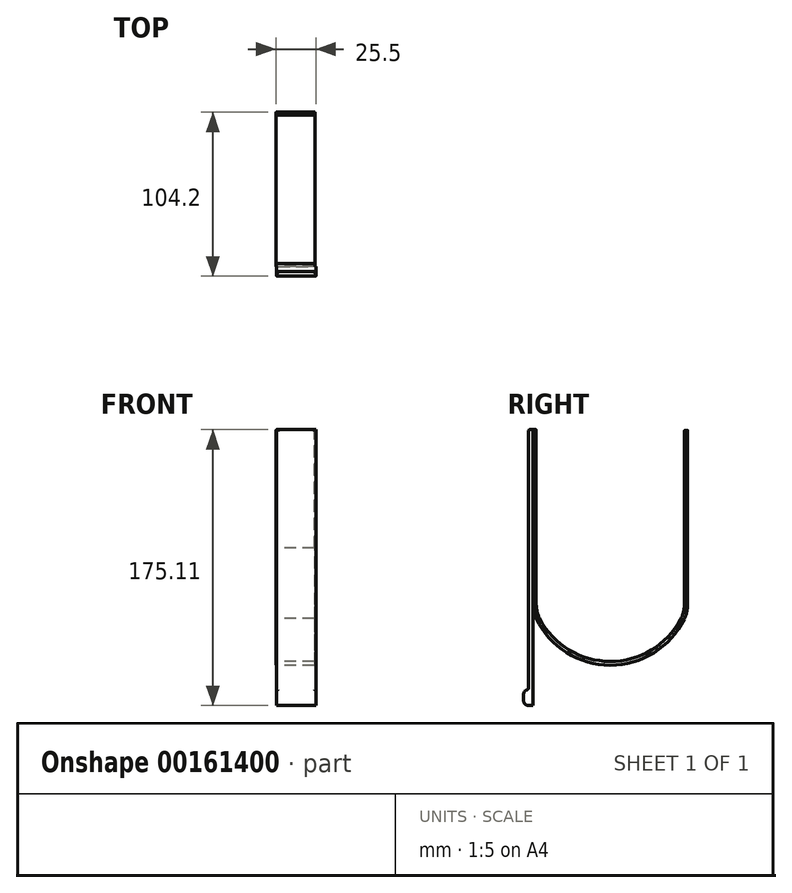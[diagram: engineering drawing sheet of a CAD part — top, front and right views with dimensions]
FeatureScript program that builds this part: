
annotation { "Feature Type Name" : "Feature", "Feature Type Description" : "" }
export const myFeature = defineFeature(function(context is Context, id is Id, definition is map)
    precondition{}
    {
        {
            var Q0;
            Q0=qCreatedBy(makeId("Right.planeOp"),FACE);
            var sketch = newSketch(context, id + "F0", { "sketchPlane" : qUnion([Q0])});
            skLineSegment(sketch, "E0.top", {"start": v(-75, -0.1) * mm, "end": v(-75, -0.1) * mm});
            skLineSegment(sketch, "E1", {"start": v(23.2, -0.2) * mm, "end": v(23.2, 74.65) * mm});
            skLineSegment(sketch, "E2", {"start": v(21.2, 17) * mm, "end": v(21.2, 74.65) * mm});
            skLineSegment(sketch, "E3", {"start": v(21.2, 74.65) * mm, "end": v(23.2, 74.65) * mm});
            skLineSegment(sketch, "E4.right", {"start": v(-73, -0.1) * mm, "end": v(-73, -0.1) * mm});
            skLineSegment(sketch, "E5.left", {"start": v(-75, -0.1) * mm, "end": v(-75, 19.67) * mm});
            skLineSegment(sketch, "E6.top", {"start": v(-75, 75.06) * mm, "end": v(-73, 75.06) * mm});
            skPoint(sketch, "E5.right.end.orphan", {"position": v(-73, -27.9) * mm});
            skPoint(sketch, "E7.orphan", {"position": v(73, 0) * mm});
            skLineSegment(sketch, "E8", {"start": v(21.2, -0.2) * mm, "end": v(21.2, 17) * mm});
            skLineSegment(sketch, "E9", {"start": v(-75, 19.67) * mm, "end": v(-75, 75.06) * mm});
            skLineSegment(sketch, "E10", {"start": v(-73, -0.1) * mm, "end": v(-73, 75.06) * mm});
            skLineSegment(sketch, "E11", {"start": v(-75, -0.1) * mm, "end": v(-75, -36.03) * mm});
            skLineSegment(sketch, "E12", {"start": v(-73, -0.1) * mm, "end": v(-73, -35.72) * mm});
            skLineSegment(sketch, "E13", {"start": v(21.11, -36.05) * mm, "end": v(21.2, -0.2) * mm});
            skLineSegment(sketch, "E14", {"start": v(23.2, -0.2) * mm, "end": v(23.11, -36.36) * mm});
            skPoint(sketch, "E15.visualSharp", {"position": v(-73, -40.17) * mm});
            skArc(sketch, "E15.filletArc", {"start": v(-73, -35.72) * mm, "mid": v(-72.4, -40.59) * mm, "end": v(-70.63, -45.16) * mm});
            skPoint(sketch, "E16.visualSharp", {"position": v(-75, -40.17) * mm});
            skArc(sketch, "E16.filletArc", {"start": v(-75, -36.03) * mm, "mid": v(-74.48, -40.55) * mm, "end": v(-72.95, -44.85) * mm});
            skPoint(sketch, "E17.visualSharp", {"position": v(21.1, -40.47) * mm});
            skArc(sketch, "E17.filletArc", {"start": v(18.75, -45.43) * mm, "mid": v(20.5, -40.88) * mm, "end": v(21.11, -36.05) * mm});
            skPoint(sketch, "E18.visualSharp", {"position": v(23.1, -40.47) * mm});
            skArc(sketch, "E18.filletArc", {"start": v(21.07, -45.11) * mm, "mid": v(22.59, -40.85) * mm, "end": v(23.11, -36.36) * mm});
            skArc(sketch, "E19", {"start": v(-70.63, -45.16) * mm, "mid": v(-26.02, -72.12) * mm, "end": v(18.75, -45.43) * mm});
            skArc(sketch, "E20", {"start": v(-72.95, -44.85) * mm, "mid": v(-26.03, -74.5) * mm, "end": v(21.07, -45.11) * mm});
            skSolve(sketch);
        }
        {
            var Q0;
            Q0 = qSketchRegion(id + "F0", true);
            extrude(context, id + "F1", {"entities" : qUnion([Q0]), "depth" : 25 * mm});
        }
        {
            var Q0;
            Q0=makeQuery(id+"F1.opExtrude","CAP_FACE",FACE,{"disambiguationData":[OSD([sQuery(id+"F0.wireOp",EDGE,"I4BVIpaZ-qeHf-sJ9Z-gygj-pwvrjwHkCjhy"),sQuery(id+"F0.wireOp",EDGE,"E1"),sQuery(id+"F0.wireOp",EDGE,"E2"),sQuery(id+"F0.wireOp",EDGE,"E3"),sQuery(id+"F0.wireOp",EDGE,"E0.top"),sQuery(id+"F0.wireOp",EDGE,"E5.left"),sQuery(id+"F0.wireOp",EDGE,"E6.top"),sQuery(id+"F0.wireOp",EDGE,"E8"),sQuery(id+"F0.wireOp",EDGE,"E9"),sQuery(id+"F0.wireOp",EDGE,"E10"),sQuery(id+"F0.wireOp",EDGE,"QJk6ctZD-O0Ay-Ia8g-pyr9-3ZWjt8AZZsZL")])],"isStart":false});
            var Q1;
            Q1=makeQuery(id+"F1.opExtrude","CAP_FACE",FACE,{"disambiguationData":[OSD([sQuery(id+"F0.wireOp",EDGE,"I4BVIpaZ-qeHf-sJ9Z-gygj-pwvrjwHkCjhy"),sQuery(id+"F0.wireOp",EDGE,"E1"),sQuery(id+"F0.wireOp",EDGE,"E2"),sQuery(id+"F0.wireOp",EDGE,"E3"),sQuery(id+"F0.wireOp",EDGE,"E0.top"),sQuery(id+"F0.wireOp",EDGE,"E5.left"),sQuery(id+"F0.wireOp",EDGE,"E6.top"),sQuery(id+"F0.wireOp",EDGE,"E8"),sQuery(id+"F0.wireOp",EDGE,"E9"),sQuery(id+"F0.wireOp",EDGE,"E10"),sQuery(id+"F0.wireOp",EDGE,"QJk6ctZD-O0Ay-Ia8g-pyr9-3ZWjt8AZZsZL")])],"isStart":true});
            fillet(context, id + "F2", {"entities" : qUnion([Q0, Q1]), "radius" : 0.5 * mm, "tangentPropagation" : true, "allowEdgeOverflow" : false});
        }
        {
            var Q0;
            Q0=makeQuery(id+"F1.opExtrude","SWEPT_FACE",FACE,{"disambiguationData":[OSD([sQuery(id+"F0.wireOp",EDGE,"E5.left"),sQuery(id+"F0.wireOp",EDGE,"E9")])]});
            var sketch = newSketch(context, id + "F3", { "sketchPlane" : qUnion([Q0])});
            skLineSegment(sketch, "E21.bottom", {"start": v(0.5, 75.06) * mm, "end": v(25.5, 75.06) * mm});
            skLineSegment(sketch, "E21.top", {"start": v(0.5, -100.05) * mm, "end": v(25.5, -100.05) * mm});
            skLineSegment(sketch, "E21.left", {"start": v(0.5, 75.06) * mm, "end": v(0.5, -100.05) * mm});
            skLineSegment(sketch, "E21.right", {"start": v(25.5, 75.06) * mm, "end": v(25.5, -100.05) * mm});
            skSolve(sketch);
        }
        {
            var Q0;
            Q0 = qSketchRegion(id + "F3", true);
            extrude(context, id + "F4", {"entities" : qUnion([Q0]), "operationType" : NewBodyOperationType.ADD, "depth" : 3 * mm});
        }
        {
            var Q0;
            Q0=makeQuery(id+"F4.opExtrude","CAP_FACE",FACE,{"disambiguationData":[OSD([sQuery(id+"F3.wireOp",EDGE,"E21.bottom"),sQuery(id+"F3.wireOp",EDGE,"E21.top"),sQuery(id+"F3.wireOp",EDGE,"E21.left"),sQuery(id+"F3.wireOp",EDGE,"E21.right")])],"isStart":false});
            var sketch = newSketch(context, id + "F5", { "sketchPlane" : qUnion([Q0])});
            skLineSegment(sketch, "E22.bottom", {"start": v(0.5, -100.05) * mm, "end": v(25.5, -100.05) * mm});
            skLineSegment(sketch, "E22.top", {"start": v(0.5, -90.05) * mm, "end": v(25.5, -90.05) * mm});
            skLineSegment(sketch, "E22.left", {"start": v(0.5, -100.05) * mm, "end": v(0.5, -90.05) * mm});
            skLineSegment(sketch, "E22.right", {"start": v(25.5, -100.05) * mm, "end": v(25.5, -90.05) * mm});
            skSolve(sketch);
        }
        {
            var Q0;
            Q0 = qSketchRegion(id + "F5", true);
            extrude(context, id + "F6", {"entities" : qUnion([Q0]), "operationType" : NewBodyOperationType.ADD, "depth" : 3 * mm});
        }
        {
            var Q0;
            Q0=makeQuery(id+"F6.opExtrude","CAP_EDGE",EDGE,{"disambiguationData":[OSD([sQuery(id+"F5.wireOp",EDGE,"E22.top")])],"isStart":false});
            var Q1;
            Q1=makeQuery(id+"F6.opExtrude","CAP_EDGE",EDGE,{"disambiguationData":[OSD([sQuery(id+"F5.wireOp",EDGE,"E22.bottom")])],"isStart":false});
            fillet(context, id + "F7", {"entities" : qUnion([Q0, Q1]), "radius" : 3 * mm, "tangentPropagation" : true, "allowEdgeOverflow" : false});
        }
        {
            var Q0;
            Q0=makeQuery(id+"F4.opExtrude","CAP_FACE",FACE,{"disambiguationData":[OSD([sQuery(id+"F3.wireOp",EDGE,"E21.bottom"),sQuery(id+"F3.wireOp",EDGE,"E21.top"),sQuery(id+"F3.wireOp",EDGE,"E21.left"),sQuery(id+"F3.wireOp",EDGE,"E21.right")])],"isStart":false});
            var Q1;
            Q1=makeQuery(id+"F4.boolean.opBoolean","SPLIT",EDGE,{"derivedFrom":makeQuery(id+"F4.opExtrude","CAP_EDGE",EDGE,{"disambiguationData":[OSD([sQuery(id+"F3.wireOp",EDGE,"E21.left")])],"isStart":true})});
            fillet(context, id + "F8", {"entities" : qUnion([Q0, Q1]), "radius" : 1 * mm, "tangentPropagation" : true, "allowEdgeOverflow" : false});
        }
    });
